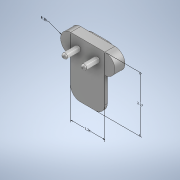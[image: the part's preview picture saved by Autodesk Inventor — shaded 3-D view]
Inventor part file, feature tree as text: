
AUTODESK INVENTOR PART (.ipt)
format: ipt  version: 2022 (Build 260153000, 153)  size: 203,264 bytes
history: native  units: in
note: dims shown in document units (in); Inventor stores cm internally (conversion verified against a paired STEP export)
features: extrude x6, sketch x6, other x4, fillet x1
ambient origin geometry x8: Origin, YZ Plane, XZ Plane, XY Plane, X Axis, Y Axis, Z Axis, Center Point
bodies: Body1 (feature_tree)
feature tree (17):
  other  "Annotations"
  extrude  "Extrusion2"  Depth=0.5906in
  extrude  "Extrusion3"  Depth=1.283in
  sketch  "Sketch4"  dims[d10=0.3937in d11=0.0in d12=0.0in]
  extrude  "Extrusion7"  TaperAngle=0.0deg  [1 undecoded]
  extrude  "Extrusion6"  Depth=0.315in
  extrude  "Extrusion8"  Depth=2.1091in
  extrude  "Extrusion9"  Depth=0.0984in
  fillet  "Fillet1"  Radius=0.3937in
  sketch  "Sketch2"  dims[d5=0.374in d6=0.5906in]
  sketch  "Sketch3"  dims[d7=0.4921in d8=0.0in d9=1.283in]
  sketch  "Sketch8"  dims[d13=0.5906in d14=0.315in]
  sketch  "Sketch10"  dims[d21=1.0in d22=0.0in d23=2.1091in]
  sketch  "Sketch11"  dims[d25=0.0591in d26=0.0984in d27=0.3937in d28=0.0in d29=0.752in d30=0.1984in d31=0.0in d32=0.0in d33=0.3937in d34=0.0in d35=0.5906in d36=0.0in d37=0.0787in d40=0.0in d41=0.0in d42=0.3937in d43=1.3386in d44=0.9639in d45=0.3933in d46=0.2945in d47=0.2237in d48=2.1681in d38=0.0in d39=0.0in]
  other  "Linear Dimension 1"
  other  "Radial Dimension 1"
  other  "Linear Dimension 2"
note: 1 required parameter value undecoded (feature->parameter linkage not recoverable at this tier; creation-order binding heuristic only, values carry confidence <= 0.55)
